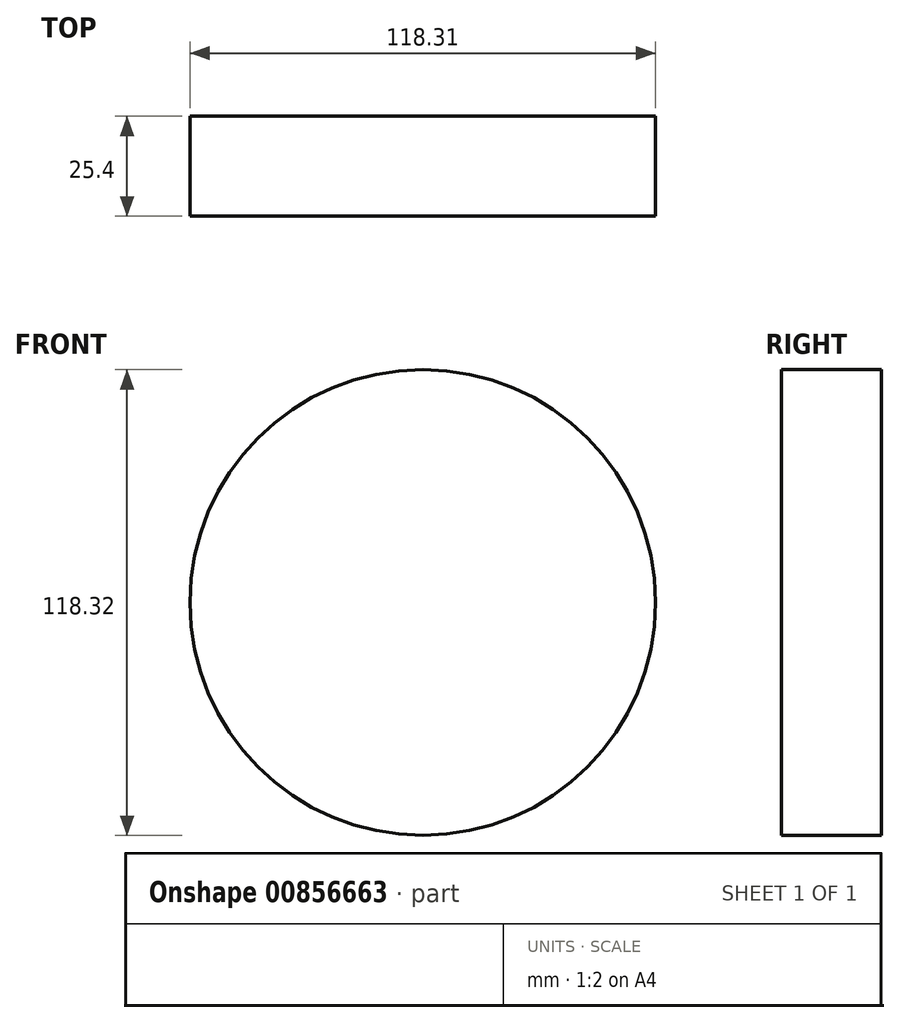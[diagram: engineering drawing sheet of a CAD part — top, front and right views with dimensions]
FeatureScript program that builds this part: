
annotation { "Feature Type Name" : "Feature", "Feature Type Description" : "" }
export const myFeature = defineFeature(function(context is Context, id is Id, definition is map)
    precondition{}
    {
        {
            var Q0;
            Q0=qCreatedBy(makeId("Front.planeOp"),FACE);
            var sketch = newSketch(context, id + "F0", { "sketchPlane" : qUnion([Q0])});
            skCircle(sketch, "E0", {"center": v(-200.56, -16.32) * mm, "radius": 59.16 * mm});
            skSolve(sketch);
        }
        {
            var Q0;
            Q0 = qSketchRegion(id + "F0", true);
            extrude(context, id + "F1", {"entities" : qUnion([Q0]), "depth" : 25.4 * mm, "offsetDistance" : 25.4 * mm});
        }
    });
